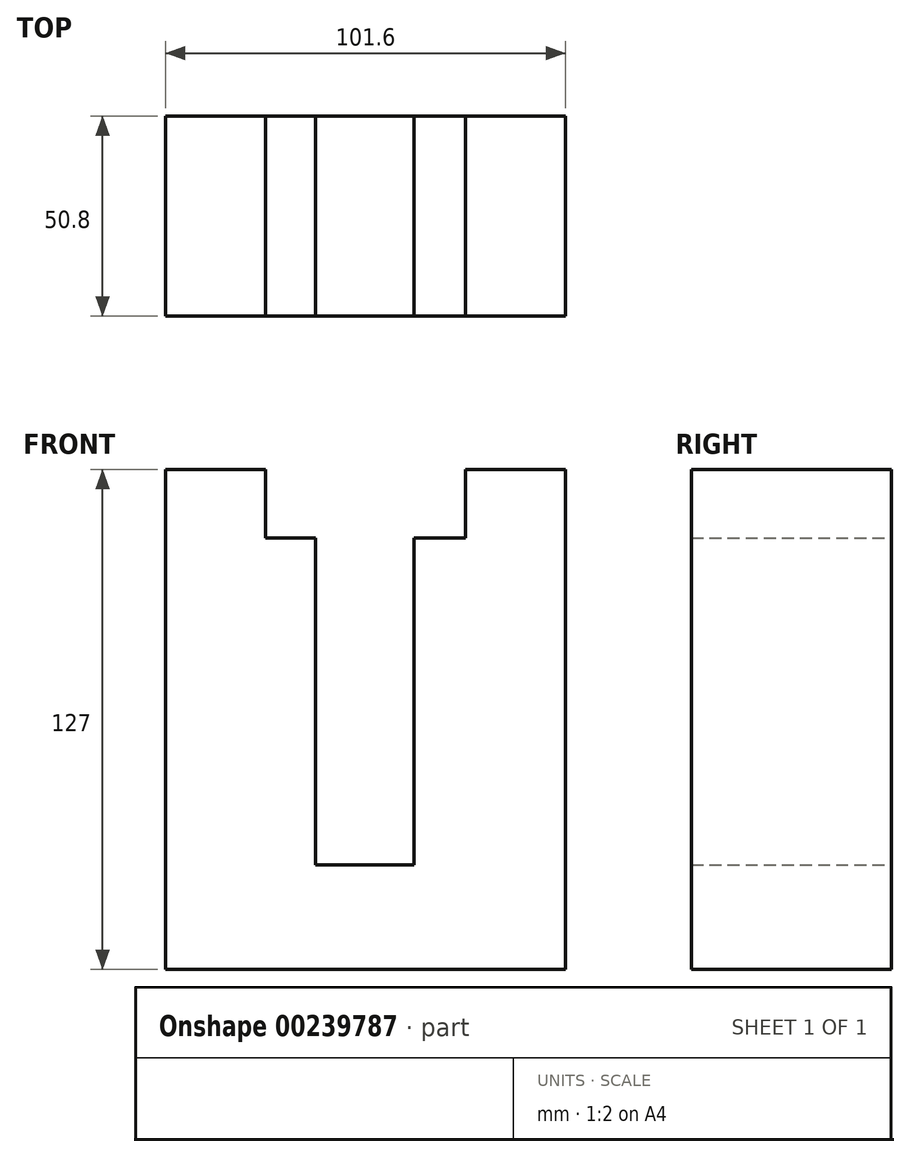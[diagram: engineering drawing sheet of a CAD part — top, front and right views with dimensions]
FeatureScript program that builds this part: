
annotation { "Feature Type Name" : "Feature", "Feature Type Description" : "" }
export const myFeature = defineFeature(function(context is Context, id is Id, definition is map)
    precondition{}
    {
        {
            var Q0;
            Q0=qCreatedBy(makeId("Front.planeOp"),FACE);
            var sketch = newSketch(context, id + "F0", { "sketchPlane" : qUnion([Q0])});
            skLineSegment(sketch, "E0.bottom", {"start": v(0, 0) * mm, "end": v(101.6, 0) * mm});
            skLineSegment(sketch, "E0.left", {"start": v(0, 0) * mm, "end": v(0, 127) * mm});
            skLineSegment(sketch, "E0.right", {"start": v(101.6, 0) * mm, "end": v(101.6, 127) * mm});
            skLineSegment(sketch, "E1", {"start": v(0, 127) * mm, "end": v(25.4, 127) * mm});
            skLineSegment(sketch, "E2", {"start": v(101.6, 127) * mm, "end": v(76.2, 127) * mm});
            skLineSegment(sketch, "E3", {"start": v(25.4, 127) * mm, "end": v(25.4, 109.6) * mm});
            skLineSegment(sketch, "E4", {"start": v(25.4, 109.6) * mm, "end": v(38.07, 109.6) * mm});
            skLineSegment(sketch, "E5", {"start": v(38.07, 109.6) * mm, "end": v(38.07, 90.55) * mm});
            skLineSegment(sketch, "E6", {"start": v(38.07, 26.55) * mm, "end": v(63.1, 26.55) * mm});
            skLineSegment(sketch, "E7", {"start": v(63.1, 90.55) * mm, "end": v(63.1, 109.6) * mm});
            skLineSegment(sketch, "E8", {"start": v(63.1, 109.6) * mm, "end": v(76.2, 109.6) * mm});
            skLineSegment(sketch, "E9", {"start": v(76.2, 109.6) * mm, "end": v(76.2, 127) * mm});
            skLineSegment(sketch, "E10", {"start": v(38.07, 90.55) * mm, "end": v(38.07, 26.55) * mm});
            skPoint(sketch, "E11.start.orphan", {"position": v(25.4, 90.55) * mm});
            skPoint(sketch, "E12.end.orphan", {"position": v(76.2, 90.55) * mm});
            skLineSegment(sketch, "E13", {"start": v(63.1, 90.55) * mm, "end": v(63.1, 26.55) * mm});
            skPoint(sketch, "E14.orphan", {"position": v(76.2, 26.55) * mm});
            skSolve(sketch);
        }
        {
            var Q0;
            Q0=makeQuery(id+"F0.imprint","IMPRINT",FACE,{"disambiguationData":[TD([[makeQuery(id+"F0.imprint","IMPRINT",EDGE,{"derivedFrom":sQuery(id+"F0.wireOp",EDGE,"E0.bottom")}),1.0]])]});
            extrude(context, id + "F1", {"entities" : qUnion([Q0]), "depth" : 50.8 * mm});
        }
        {
            var Q0;
            Q0=makeQuery(id+"F1.opExtrude","SWEPT_FACE",FACE,{"disambiguationData":[OSD([sQuery(id+"F0.wireOp",EDGE,"E6")])]});
            var sketch = newSketch(context, id + "F2", { "sketchPlane" : qUnion([Q0])});
            skCircle(sketch, "E15", {"center": v(50.59, -24.2) * mm, "radius": 19.64 * mm});
            skPoint(sketch, "E15.centerSnap0", {"position": v(50.59, 0) * mm});
            skSolve(sketch);
        }
        {
            var Q0;
            Q0=makeQuery(id+"F2.imprint","IMPRINT",FACE,{"disambiguationData":[TD([[makeQuery(id+"F2.imprint","IMPRINT",EDGE,{"derivedFrom":sQuery(id+"F2.wireOp",EDGE,"E15")}),1.0]])]});
            extrude(context, id + "F3", {"entities" : qUnion([Q0]), "operationType" : NewBodyOperationType.REMOVE, "depth" : 508 * mm});
        }
    });
